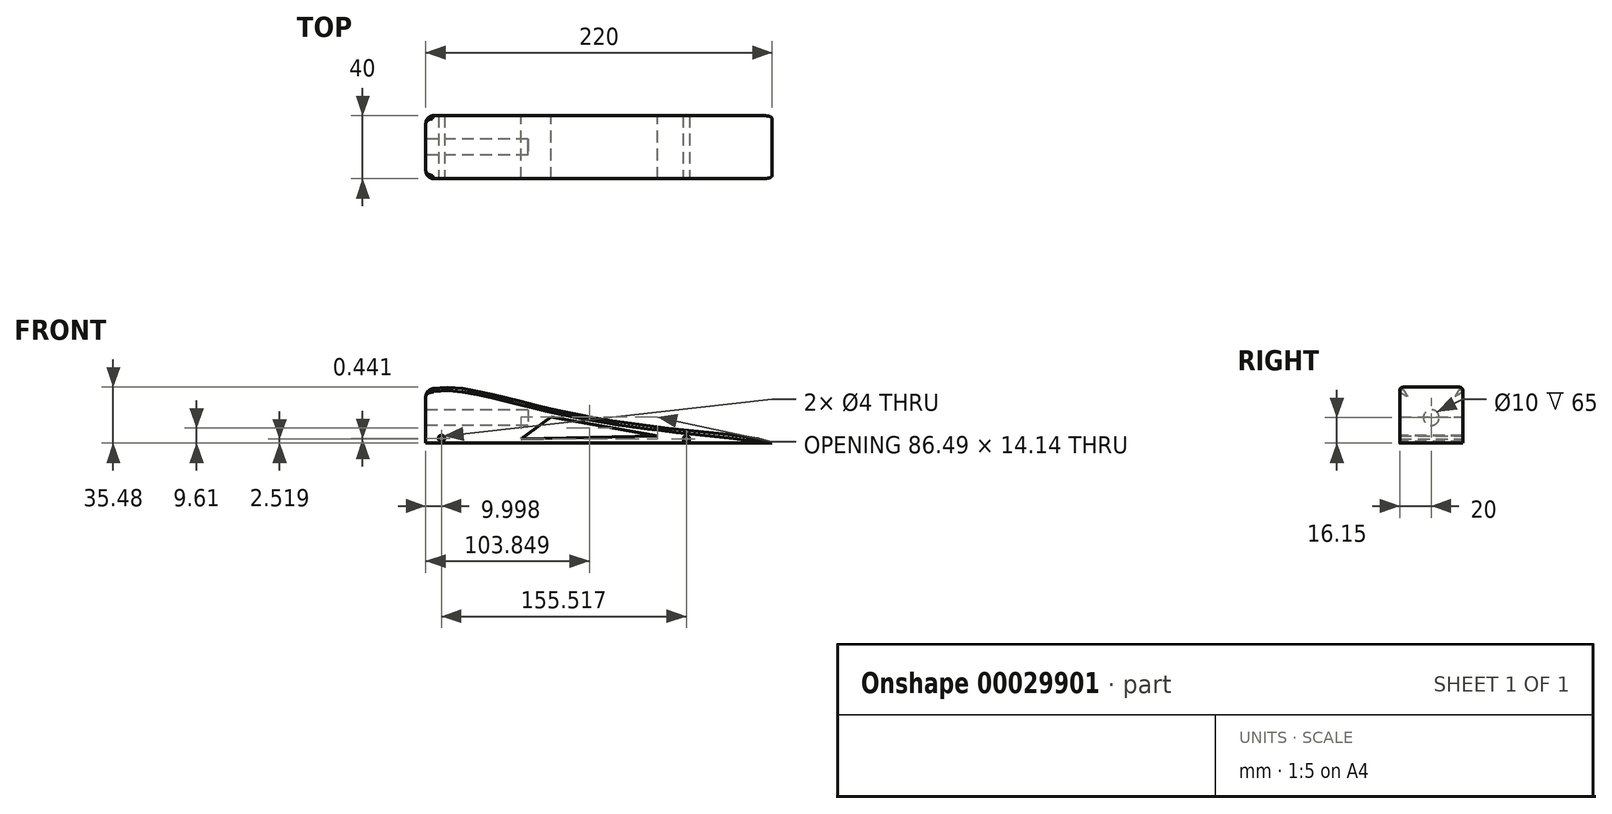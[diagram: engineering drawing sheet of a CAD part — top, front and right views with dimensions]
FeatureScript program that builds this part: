
annotation { "Feature Type Name" : "Feature", "Feature Type Description" : "" }
export const myFeature = defineFeature(function(context is Context, id is Id, definition is map)
    precondition{}
    {
        {
            var Q0;
            Q0=qCreatedBy(makeId("Front.planeOp"),FACE);
            var sketch = newSketch(context, id + "F0", { "sketchPlane" : qUnion([Q0])});
            skLineSegment(sketch, "E0.bottom", {"start": v(-84.2, -32.3) * mm, "end": v(135.8, -32.3) * mm});
            skLineSegment(sketch, "E0.top", {"start": v(-84.2, 37.7) * mm, "end": v(135.8, 37.7) * mm});
            skLineSegment(sketch, "E0.left", {"start": v(-84.2, -32.3) * mm, "end": v(-84.2, 37.7) * mm});
            skLineSegment(sketch, "E0.right", {"start": v(135.8, -32.3) * mm, "end": v(135.8, 37.7) * mm});
            skFitSpline(sketch, "E1", {"points": [v(135.8, -32.3) * mm, v(98.07, -25.93) * mm, v(-3.45, -10.88) * mm, v(-84.2, 0) * mm, v(-84.2, -32.3) * mm], "startDerivative": vector(-92.66, 45.29) * mm, "endDerivative": vector(49.78, -207.58) * mm});
            skLineSegment(sketch, "E2", {"start": v(-23.6, -29.76) * mm, "end": v(62.9, -27.64) * mm});
            skLineSegment(sketch, "E3", {"start": v(-23.6, -29.76) * mm, "end": v(-4.74, -15.62) * mm});
            skLineSegment(sketch, "E4", {"start": v(-4.74, -15.62) * mm, "end": v(62.9, -27.64) * mm});
            skSolve(sketch);
        }
        {
            var Q0;
            Q0=makeQuery(id+"F0.imprint","IMPRINT",FACE,{"disambiguationData":[TD([[makeQuery(id+"F0.imprint","IMPRINT",EDGE,{"derivedFrom":sQuery(id+"F0.wireOp",EDGE,"E0.bottom")}),1.0]])]});
            extrude(context, id + "F1", {"entities" : qUnion([Q0]), "depth" : 40 * mm});
        }
        {
            var Q0;
            Q0=makeQuery(id+"F1.opExtrude","SWEPT_FACE",FACE,{"disambiguationData":[OSD([sQuery(id+"F0.wireOp",EDGE,"E0.left")])]});
            var sketch = newSketch(context, id + "F2", { "sketchPlane" : qUnion([Q0])});
            skCircle(sketch, "E5", {"center": v(20, -16.15) * mm, "radius": 5 * mm});
            skSolve(sketch);
        }
        {
            var Q0;
            Q0=makeQuery(id+"F2.imprint","IMPRINT",FACE,{"disambiguationData":[TD([[makeQuery(id+"F2.imprint","IMPRINT",EDGE,{"derivedFrom":sQuery(id+"F2.wireOp",EDGE,"E5")}),1.0]])]});
            extrude(context, id + "F3", {"entities" : qUnion([Q0]), "operationType" : NewBodyOperationType.REMOVE, "oppositeDirection" : true, "depth" : 65 * mm});
        }
        {
            var Q0;
            Q0=makeQuery(id+"F1.opExtrude","CAP_EDGE",EDGE,{"disambiguationData":[OSD([sQuery(id+"F0.wireOp",EDGE,"E1")])],"isStart":true});
            var Q1;
            Q1=makeQuery(id+"F1.opExtrude","CAP_EDGE",EDGE,{"disambiguationData":[OSD([sQuery(id+"F0.wireOp",EDGE,"E1")])],"isStart":false});
            fillet(context, id + "F4", {"entities" : qUnion([Q0, Q1]), "radius" : 2 * mm, "tangentPropagation" : true, "allowEdgeOverflow" : false});
        }
        {
            var Q0;
            Q0=makeQuery(id+"F1.opExtrude","CAP_FACE",FACE,{"disambiguationData":[OSD([sQuery(id+"F0.wireOp",EDGE,"E0.bottom"),sQuery(id+"F0.wireOp",EDGE,"E0.left"),sQuery(id+"F0.wireOp",EDGE,"E1")])],"isStart":false});
            var sketch = newSketch(context, id + "F5", { "sketchPlane" : qUnion([Q0])});
            skCircle(sketch, "E6", {"center": v(81.31, -29.78) * mm, "radius": 2 * mm});
            skCircle(sketch, "E7", {"center": v(-74.2, -29.34) * mm, "radius": 2 * mm});
            skSolve(sketch);
        }
        {
            var Q0;
            Q0=makeQuery(id+"F5.imprint","IMPRINT",FACE,{"disambiguationData":[TD([[makeQuery(id+"F5.imprint","IMPRINT",EDGE,{"derivedFrom":sQuery(id+"F5.wireOp",EDGE,"E7")}),1.0]])]});
            var Q1;
            Q1=makeQuery(id+"F5.imprint","IMPRINT",FACE,{"disambiguationData":[TD([[makeQuery(id+"F5.imprint","IMPRINT",EDGE,{"derivedFrom":sQuery(id+"F5.wireOp",EDGE,"E6")}),1.0]])]});
            extrude(context, id + "F6", {"entities" : qUnion([Q0, Q1]), "operationType" : NewBodyOperationType.REMOVE, "endBound" : BoundingType.THROUGH_ALL, "oppositeDirection" : true, "depth" : 25 * mm});
        }
        {
            var Q0;
            Q0=makeQuery(id+"F1.opExtrude","CAP_EDGE",EDGE,{"disambiguationData":[OSD([sQuery(id+"F0.wireOp",EDGE,"E0.left")])],"isStart":false});
            var Q1;
            Q1=makeQuery(id+"F1.opExtrude","CAP_EDGE",EDGE,{"disambiguationData":[OSD([sQuery(id+"F0.wireOp",EDGE,"E0.left")])],"isStart":true});
            fillet(context, id + "F7", {"entities" : qUnion([Q0, Q1]), "radius" : 5 * mm, "tangentPropagation" : true, "allowEdgeOverflow" : false});
        }
    });
